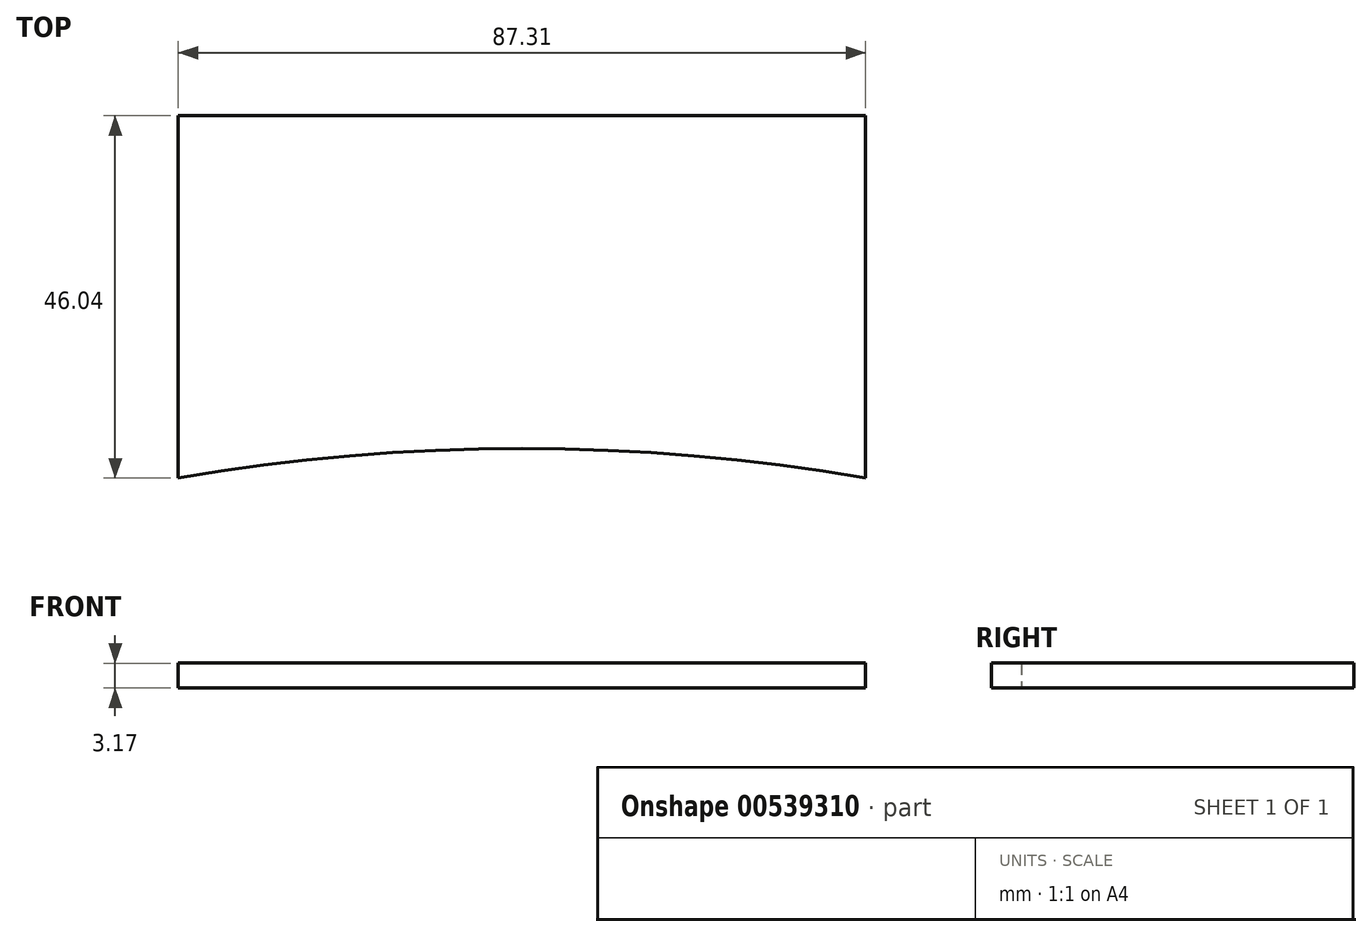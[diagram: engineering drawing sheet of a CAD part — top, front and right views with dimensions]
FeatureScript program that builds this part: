
annotation { "Feature Type Name" : "Feature", "Feature Type Description" : "" }
export const myFeature = defineFeature(function(context is Context, id is Id, definition is map)
    precondition{}
    {
        {
            var Q0;
            Q0=qCreatedBy(makeId("Top.planeOp"),FACE);
            var sketch = newSketch(context, id + "F0", { "sketchPlane" : qUnion([Q0])});
            skLineSegment(sketch, "E0.bottom", {"start": v(-305.78, 36.42) * mm, "end": v(-218.47, 36.42) * mm});
            skLineSegment(sketch, "E0.top", {"start": v(-305.78, -9.62) * mm, "end": v(-218.47, -9.62) * mm, "construction": true});
            skLineSegment(sketch, "E0.left", {"start": v(-305.78, 36.42) * mm, "end": v(-305.78, -9.62) * mm});
            skLineSegment(sketch, "E0.right", {"start": v(-218.47, 36.42) * mm, "end": v(-218.47, -9.62) * mm});
            skPoint(sketch, "E0.middle", {"position": v(-262.13, 13.4) * mm});
            skLineSegment(sketch, "E1", {"start": v(-305.78, -9.62) * mm, "end": v(-305.78, -9.62) * mm});
            skArc(sketch, "E2", {"start": v(-218.47, -9.62) * mm, "mid": v(-262.13, -5.84) * mm, "end": v(-305.78, -9.62) * mm});
            skArc(sketch, "E3", {"start": v(-305.78, -9.62) * mm, "mid": v(-262.13, -513.84) * mm, "end": v(-218.47, -9.62) * mm, "construction": true});
            skLineSegment(sketch, "E4.bottom", {"start": v(-231.95, 44.94) * mm, "end": v(-282.75, 44.94) * mm, "construction": true});
            skLineSegment(sketch, "E4.top", {"start": v(-231.95, 76.7) * mm, "end": v(-282.75, 76.7) * mm, "construction": true});
            skLineSegment(sketch, "E4.left", {"start": v(-231.95, 44.94) * mm, "end": v(-231.95, 76.7) * mm, "construction": true});
            skLineSegment(sketch, "E4.right", {"start": v(-282.75, 44.94) * mm, "end": v(-282.75, 76.7) * mm, "construction": true});
            skPoint(sketch, "E4.middle", {"position": v(-257.35, 60.82) * mm});
            skPoint(sketch, "E5", {"position": v(-305.78, 36.45) * mm});
            skPoint(sketch, "E6", {"position": v(-231.95, 57.64) * mm});
            skArc(sketch, "E7", {"start": v(-231.95, 57.64) * mm, "mid": v(-235.67, 48.66) * mm, "end": v(-244.65, 44.94) * mm});
            skArc(sketch, "E8", {"start": v(-271.63, 44.94) * mm, "mid": v(-279.5, 48.2) * mm, "end": v(-282.75, 56.05) * mm});
            skArc(sketch, "E9", {"start": v(-282.75, 61.95) * mm, "mid": v(-279.56, 70.94) * mm, "end": v(-271.43, 75.92) * mm});
            skArc(sketch, "E10", {"start": v(-271.43, 75.92) * mm, "mid": v(-267.8, 76.5) * mm, "end": v(-264.13, 76.7) * mm});
            skSolve(sketch);
        }
        {
            var Q0;
            Q0 = qSketchRegion(id + "F0", true);
            extrude(context, id + "F1", {"entities" : qUnion([Q0]), "depth" : 3.17 * mm, "offsetDistance" : 25.4 * mm});
        }
    });
